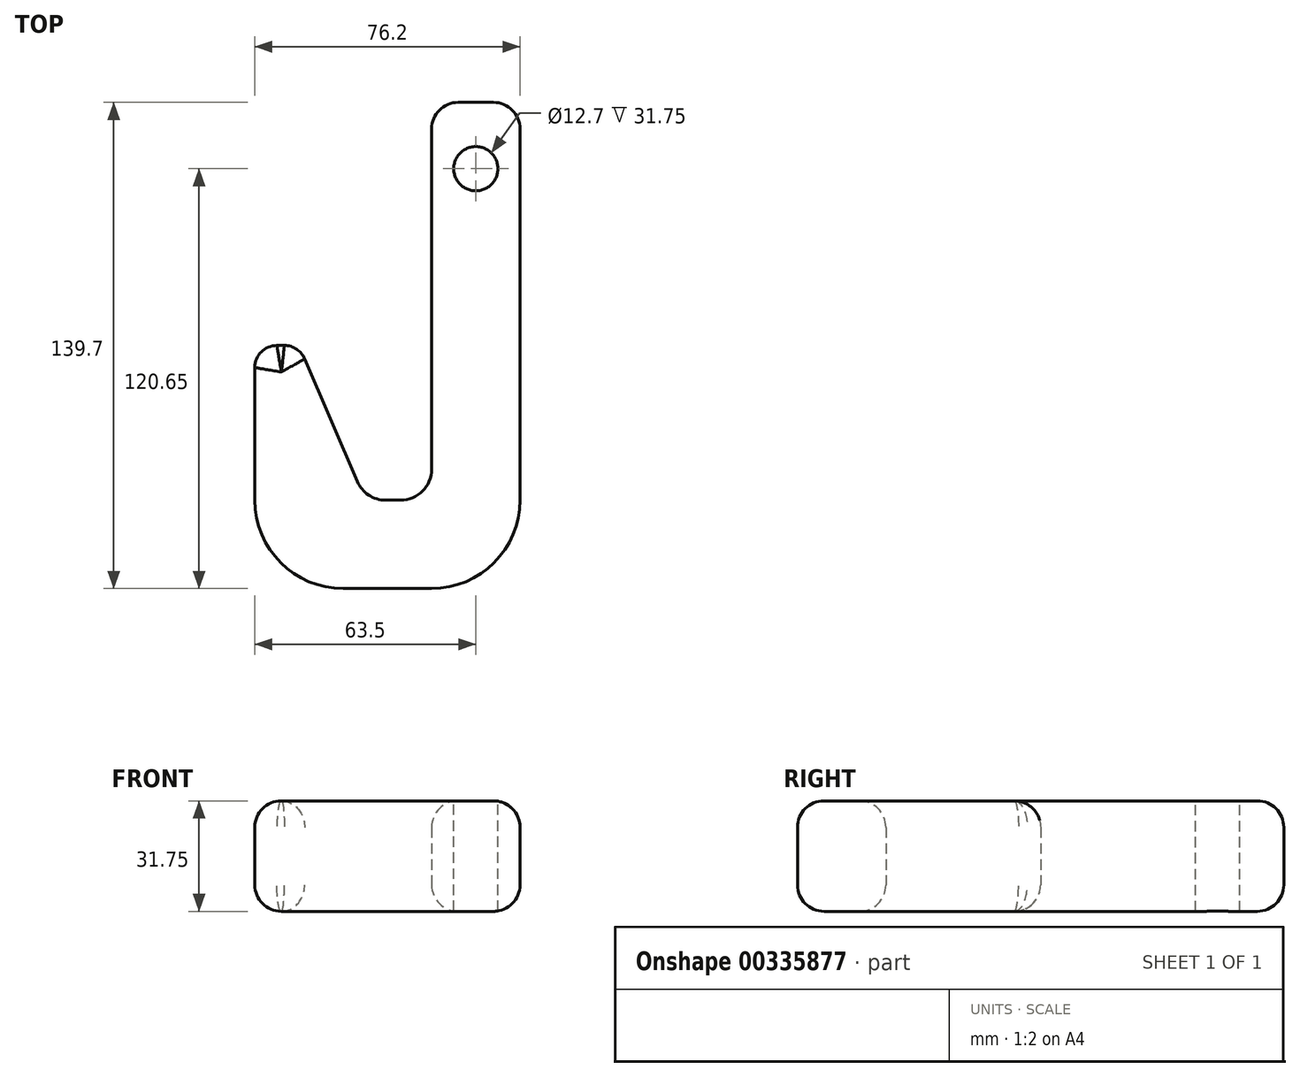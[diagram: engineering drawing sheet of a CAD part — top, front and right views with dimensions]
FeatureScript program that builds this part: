
annotation { "Feature Type Name" : "Feature", "Feature Type Description" : "" }
export const myFeature = defineFeature(function(context is Context, id is Id, definition is map)
    precondition{}
    {
        {
            var Q0;
            Q0=qCreatedBy(makeId("Top.planeOp"),FACE);
            var sketch = newSketch(context, id + "F0", { "sketchPlane" : qUnion([Q0])});
            skLineSegment(sketch, "E0", {"start": v(0, 0) * mm, "end": v(76.2, 0) * mm});
            skLineSegment(sketch, "E1", {"start": v(76.2, 0) * mm, "end": v(76.2, 139.7) * mm});
            skLineSegment(sketch, "E2", {"start": v(76.2, 139.7) * mm, "end": v(50.8, 139.7) * mm});
            skLineSegment(sketch, "E3", {"start": v(50.8, 139.7) * mm, "end": v(50.8, 25.4) * mm});
            skLineSegment(sketch, "E4", {"start": v(50.8, 25.4) * mm, "end": v(31.75, 25.4) * mm});
            skLineSegment(sketch, "E5", {"start": v(12.7, 69.85) * mm, "end": v(0, 69.85) * mm});
            skLineSegment(sketch, "E6", {"start": v(0, 69.85) * mm, "end": v(0, 0) * mm});
            skLineSegment(sketch, "E7", {"start": v(31.75, 25.4) * mm, "end": v(12.7, 69.85) * mm});
            skSolve(sketch);
        }
        {
            var Q0;
            Q0 = qSketchRegion(id + "F0", true);
            extrude(context, id + "F1", {"entities" : qUnion([Q0]), "depth" : 31.75 * mm});
        }
        {
            var Q0;
            Q0=makeQuery(id+"F1.opExtrude","SWEPT_EDGE",EDGE,{"disambiguationData":[OSD([sQuery(id+"F0.wireOp",EDGE,"E0"),sQuery(id+"F0.wireOp",EDGE,"E6")])]});
            var Q1;
            Q1=makeQuery(id+"F1.opExtrude","SWEPT_EDGE",EDGE,{"disambiguationData":[OSD([sQuery(id+"F0.wireOp",EDGE,"E0"),sQuery(id+"F0.wireOp",EDGE,"E1")])]});
            fillet(context, id + "F2", {"entities" : qUnion([Q0, Q1]), "radius" : 25.4 * mm, "allowEdgeOverflow" : false});
        }
        {
            var Q0;
            Q0=makeQuery(id+"F1.opExtrude","SWEPT_EDGE",EDGE,{"disambiguationData":[OSD([sQuery(id+"F0.wireOp",EDGE,"E3"),sQuery(id+"F0.wireOp",EDGE,"E4")])]});
            var Q1;
            Q1=makeQuery(id+"F1.opExtrude","SWEPT_EDGE",EDGE,{"disambiguationData":[OSD([sQuery(id+"F0.wireOp",EDGE,"E4"),sQuery(id+"F0.wireOp",EDGE,"E7")])]});
            fillet(context, id + "F3", {"entities" : qUnion([Q0, Q1]), "radius" : 8.9 * mm, "tangentPropagation" : true, "allowEdgeOverflow" : false});
        }
        {
            var Q0;
            Q0=makeQuery(id+"F1.opExtrude","SWEPT_EDGE",EDGE,{"disambiguationData":[OSD([sQuery(id+"F0.wireOp",EDGE,"E5"),sQuery(id+"F0.wireOp",EDGE,"E7")])]});
            var Q1;
            Q1=makeQuery(id+"F1.opExtrude","SWEPT_EDGE",EDGE,{"disambiguationData":[OSD([sQuery(id+"F0.wireOp",EDGE,"E5"),sQuery(id+"F0.wireOp",EDGE,"E6")])]});
            fillet(context, id + "F4", {"entities" : qUnion([Q0, Q1]), "radius" : 6.35 * mm, "tangentPropagation" : true, "allowEdgeOverflow" : false});
        }
        {
            var Q0;
            {var subQ0=sQuery(id+"F0.wireOp",EDGE,"E5");Q0=makeQuery(id+"F4.opFillet","BLEND_EDGE",EDGE,{"blendedFrom":[makeQuery(id+"F1.opExtrude","SWEPT_EDGE",EDGE,{"disambiguationData":[OSD([subQ0,sQuery(id+"F0.wireOp",EDGE,"E6")])]}),makeQuery(id+"F1.opExtrude","SWEPT_FACE",FACE,{"disambiguationData":[OSD([subQ0])]})],"blendedInto":[makeQuery(id+"F1.opExtrude","SWEPT_FACE",FACE,{"disambiguationData":[OSD([subQ0])]})]});}
            var Q1;
            Q1=makeQuery(id+"F1.opExtrude","SWEPT_EDGE",EDGE,{"disambiguationData":[OSD([sQuery(id+"F0.wireOp",EDGE,"E2"),sQuery(id+"F0.wireOp",EDGE,"E3")])]});
            var Q2;
            Q2=makeQuery(id+"F1.opExtrude","SWEPT_EDGE",EDGE,{"disambiguationData":[OSD([sQuery(id+"F0.wireOp",EDGE,"E1"),sQuery(id+"F0.wireOp",EDGE,"E2")])]});
            var Q3;
            Q3=makeQuery(id+"F1.opExtrude","CAP_FACE",FACE,{"disambiguationData":[OSD([sQuery(id+"F0.wireOp",EDGE,"E0"),sQuery(id+"F0.wireOp",EDGE,"E1"),sQuery(id+"F0.wireOp",EDGE,"E2"),sQuery(id+"F0.wireOp",EDGE,"E3"),sQuery(id+"F0.wireOp",EDGE,"E4"),sQuery(id+"F0.wireOp",EDGE,"E5"),sQuery(id+"F0.wireOp",EDGE,"E6"),sQuery(id+"F0.wireOp",EDGE,"E7")])],"isStart":false});
            var Q4;
            Q4=makeQuery(id+"F1.opExtrude","CAP_FACE",FACE,{"disambiguationData":[OSD([sQuery(id+"F0.wireOp",EDGE,"E0"),sQuery(id+"F0.wireOp",EDGE,"E1"),sQuery(id+"F0.wireOp",EDGE,"E2"),sQuery(id+"F0.wireOp",EDGE,"E3"),sQuery(id+"F0.wireOp",EDGE,"E4"),sQuery(id+"F0.wireOp",EDGE,"E5"),sQuery(id+"F0.wireOp",EDGE,"E6"),sQuery(id+"F0.wireOp",EDGE,"E7")])],"isStart":true});
            fillet(context, id + "F5", {"entities" : qUnion([Q0, Q1, Q2, Q3, Q4]), "radius" : 7.62 * mm, "tangentPropagation" : true, "allowEdgeOverflow" : false});
        }
        {
            var Q0;
            Q0=makeQuery(id+"F1.opExtrude","CAP_FACE",FACE,{"disambiguationData":[OSD([sQuery(id+"F0.wireOp",EDGE,"E0"),sQuery(id+"F0.wireOp",EDGE,"E1"),sQuery(id+"F0.wireOp",EDGE,"E2"),sQuery(id+"F0.wireOp",EDGE,"E3"),sQuery(id+"F0.wireOp",EDGE,"E4"),sQuery(id+"F0.wireOp",EDGE,"E5"),sQuery(id+"F0.wireOp",EDGE,"E6"),sQuery(id+"F0.wireOp",EDGE,"E7")])],"isStart":false});
            var sketch = newSketch(context, id + "F6", { "sketchPlane" : qUnion([Q0])});
            skCircle(sketch, "E8", {"center": v(63.5, 120.65) * mm, "radius": 6.35 * mm});
            skLineSegment(sketch, "E9", {"start": v(63.5, 132.08) * mm, "end": v(63.5, 101.57) * mm, "construction": true});
            skSolve(sketch);
        }
        {
            var Q0;
            Q0 = qSketchRegion(id + "F6", true);
            var Q1;
            Q1=makeQuery(id+"F1.opExtrude","CAP_FACE",FACE,{"disambiguationData":[OSD([sQuery(id+"F0.wireOp",EDGE,"E0"),sQuery(id+"F0.wireOp",EDGE,"E1"),sQuery(id+"F0.wireOp",EDGE,"E2"),sQuery(id+"F0.wireOp",EDGE,"E3"),sQuery(id+"F0.wireOp",EDGE,"E4"),sQuery(id+"F0.wireOp",EDGE,"E5"),sQuery(id+"F0.wireOp",EDGE,"E6"),sQuery(id+"F0.wireOp",EDGE,"E7")])],"isStart":true});
            extrude(context, id + "F7", {"entities" : qUnion([Q0]), "operationType" : NewBodyOperationType.REMOVE, "endBound" : BoundingType.UP_TO_SURFACE, "oppositeDirection" : true, "endBoundEntityFace" : qUnion([Q1]), "depth" : 25.4 * mm});
        }
    });
